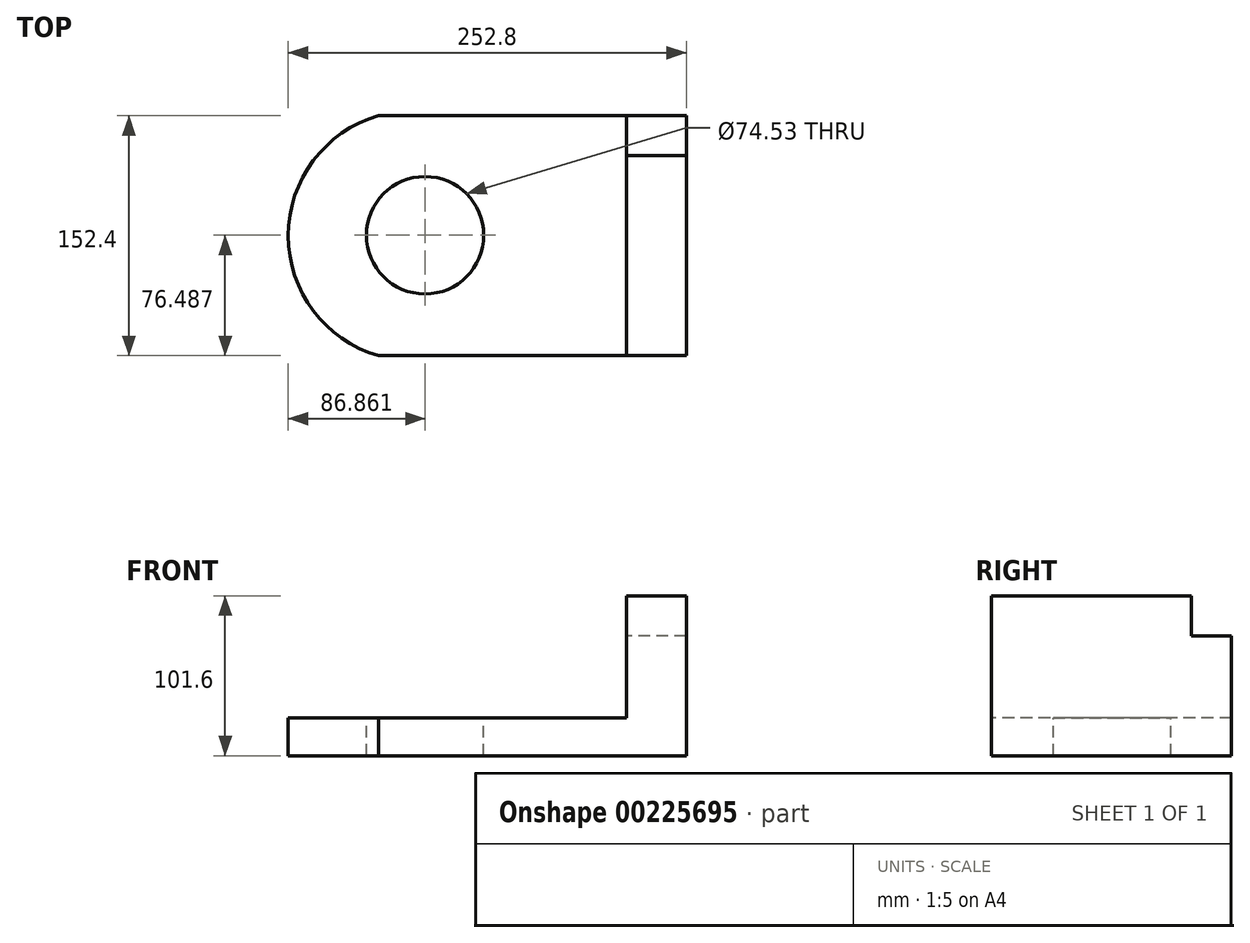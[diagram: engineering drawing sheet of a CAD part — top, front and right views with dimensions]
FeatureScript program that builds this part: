
annotation { "Feature Type Name" : "Feature", "Feature Type Description" : "" }
export const myFeature = defineFeature(function(context is Context, id is Id, definition is map)
    precondition{}
    {
        {
            var Q0;
            Q0=qCreatedBy(makeId("Top.planeOp"),FACE);
            var sketch = newSketch(context, id + "F0", { "sketchPlane" : qUnion([Q0])});
            skLineSegment(sketch, "E0.bottom", {"start": v(-15, 124.3) * mm, "end": v(239, 124.3) * mm});
            skLineSegment(sketch, "E0.top", {"start": v(-15, -28.1) * mm, "end": v(239, -28.1) * mm});
            skLineSegment(sketch, "E0.left", {"start": v(-15, 124.3) * mm, "end": v(-15, -28.1) * mm});
            skLineSegment(sketch, "E0.right", {"start": v(239, 124.3) * mm, "end": v(239, -28.1) * mm});
            skSolve(sketch);
        }
        {
            var Q0;
            Q0=makeQuery(id+"F0.imprint","IMPRINT",FACE,{"disambiguationData":[TD([[makeQuery(id+"F0.imprint","IMPRINT",EDGE,{"derivedFrom":sQuery(id+"F0.wireOp",EDGE,"E0.bottom")}),-1.0]])]});
            extrude(context, id + "F1", {"entities" : qUnion([Q0]), "depth" : 101.6 * mm});
        }
        {
            var Q0;
            Q0=makeQuery(id+"F1.opExtrude","SWEPT_FACE",FACE,{"disambiguationData":[OSD([sQuery(id+"F0.wireOp",EDGE,"E0.left")])]});
            var sketch = newSketch(context, id + "F2", { "sketchPlane" : qUnion([Q0])});
            skLineSegment(sketch, "E1.bottom", {"start": v(-124.3, 101.6) * mm, "end": v(28.1, 101.6) * mm});
            skLineSegment(sketch, "E1.top", {"start": v(-124.3, 23.92) * mm, "end": v(28.1, 23.92) * mm});
            skLineSegment(sketch, "E1.left", {"start": v(-124.3, 101.6) * mm, "end": v(-124.3, 23.92) * mm});
            skLineSegment(sketch, "E1.right", {"start": v(28.1, 101.6) * mm, "end": v(28.1, 23.92) * mm});
            skSolve(sketch);
        }
        {
            var Q0;
            Q0=makeQuery(id+"F2.imprint","IMPRINT",FACE,{"disambiguationData":[TD([[makeQuery(id+"F2.imprint","IMPRINT",EDGE,{"derivedFrom":sQuery(id+"F2.wireOp",EDGE,"E1.bottom")}),-1.0]])]});
            extrude(context, id + "F3", {"entities" : qUnion([Q0]), "operationType" : NewBodyOperationType.REMOVE, "oppositeDirection" : true, "depth" : 215.9 * mm});
        }
        {
            var Q0;
            Q0=makeQuery(id+"F3.boolean.opBoolean","COPY",FACE,{"derivedFrom":makeQuery(id+"F3.opExtrude","CAP_FACE",FACE,{"disambiguationData":[OSD([sQuery(id+"F2.wireOp",EDGE,"E1.bottom"),sQuery(id+"F2.wireOp",EDGE,"E1.top"),sQuery(id+"F2.wireOp",EDGE,"E1.left"),sQuery(id+"F2.wireOp",EDGE,"E1.right")])],"isStart":false})});
            var sketch = newSketch(context, id + "F4", { "sketchPlane" : qUnion([Q0])});
            skLineSegment(sketch, "E2.bottom", {"start": v(-124.3, 101.6) * mm, "end": v(-98.9, 101.6) * mm});
            skLineSegment(sketch, "E2.top", {"start": v(-124.3, 76.2) * mm, "end": v(-98.9, 76.2) * mm});
            skLineSegment(sketch, "E2.left", {"start": v(-124.3, 101.6) * mm, "end": v(-124.3, 76.2) * mm});
            skLineSegment(sketch, "E2.right", {"start": v(-98.9, 101.6) * mm, "end": v(-98.9, 76.2) * mm});
            skSolve(sketch);
        }
        {
            var Q0;
            Q0=makeQuery(id+"F4.imprint","IMPRINT",FACE,{"disambiguationData":[TD([[makeQuery(id+"F4.imprint","IMPRINT",EDGE,{"derivedFrom":sQuery(id+"F4.wireOp",EDGE,"E2.bottom")}),-1.0]])]});
            extrude(context, id + "F5", {"entities" : qUnion([Q0]), "operationType" : NewBodyOperationType.REMOVE, "oppositeDirection" : true, "depth" : 50.8 * mm});
        }
        {
            var Q0;
            Q0=makeQuery(id+"F3.boolean.opBoolean","COPY",FACE,{"derivedFrom":makeQuery(id+"F3.opExtrude","SWEPT_FACE",FACE,{"disambiguationData":[OSD([sQuery(id+"F2.wireOp",EDGE,"E1.top")])]})});
            var sketch = newSketch(context, id + "F6", { "sketchPlane" : qUnion([Q0])});
            skCircle(sketch, "E3", {"center": v(73.06, 48.39) * mm, "radius": 37.27 * mm});
            skSolve(sketch);
        }
        {
            var Q0;
            Q0=makeQuery(id+"F3.boolean.opBoolean","COPY",FACE,{"derivedFrom":makeQuery(id+"F3.opExtrude","SWEPT_FACE",FACE,{"disambiguationData":[OSD([sQuery(id+"F2.wireOp",EDGE,"E1.top")])]})});
            var sketch = newSketch(context, id + "F7", { "sketchPlane" : qUnion([Q0])});
            skArc(sketch, "E4", {"start": v(43.42, 124.3) * mm, "mid": v(-13.8, 48.1) * mm, "end": v(43.42, -28.1) * mm});
            skSolve(sketch);
        }
        {
            var Q0;
            {var subQ0=sQuery(id+"F7.wireOp",EDGE,"E4");Q0=makeQuery(id+"F7.imprint","IMPRINT",FACE,{"disambiguationData":[TD([[makeQuery(id+"F7.imprint","IMPRINT",EDGE,{"derivedFrom":subQ0}),-1.0]])]});}
            extrude(context, id + "F8", {"entities" : qUnion([Q0]), "operationType" : NewBodyOperationType.REMOVE, "oppositeDirection" : true, "depth" : 25.4 * mm});
        }
        {
            var Q0;
            Q0=makeQuery(id+"F6.imprint","IMPRINT",FACE,{"disambiguationData":[TD([[makeQuery(id+"F6.imprint","IMPRINT",EDGE,{"derivedFrom":sQuery(id+"F6.wireOp",EDGE,"E3")}),1.0]])]});
            extrude(context, id + "F9", {"entities" : qUnion([Q0]), "operationType" : NewBodyOperationType.REMOVE, "oppositeDirection" : true, "depth" : 25.4 * mm});
        }
    });
